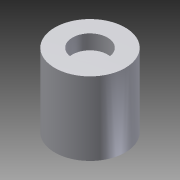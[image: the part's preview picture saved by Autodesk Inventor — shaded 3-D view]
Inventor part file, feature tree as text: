
AUTODESK INVENTOR PART (.ipt)
format: ipt  version: 2014 SP1 (Build 180222100, 222)  size: 105,472 bytes
history: native  units: mm
features: extrude x7, sketch x7
ambient origin geometry x8: Origin, YZ Plane, XZ Plane, XY Plane, X Axis, Y Axis, Z Axis, Center Point
bodies: Solid1 (feature_tree)
feature tree (14):
  extrude  "Extrusion1"  Depth=15.0mm TaperAngle=0.0deg
  extrude  "Extrusion2"  Depth=7.0mm TaperAngle=0.0deg
  extrude  "Extrusion3"  Depth=2.5mm TaperAngle=0.0deg
  extrude  "Extrusion4"  Depth=15.0mm TaperAngle=0.0deg
  extrude  "Extrusion5"  Depth=17.5mm TaperAngle=0.0deg
  extrude  "Extrusion6"  [1 undecoded]
  extrude  "Extrusion7"  [1 undecoded]
  sketch  "Sketch1"  dims[d0=12.0mm d1=15.0mm d2=0.0mm]
  sketch  "Sketch2"  dims[d3=9.398mm d4=7.0mm d5=0.0mm]
  sketch  "Sketch3"  dims[d6=6.0mm d7=2.5mm d8=0.0mm]
  sketch  "Sketch4"  dims[d9=15.0mm d10=0.0mm d11=15.0mm d12=0.0mm]
  sketch  "Sketch5"  dims[d13=17.5mm d14=0.0mm d15=17.5mm d16=0.0mm]
  sketch  "Sketch6"
  sketch  "Sketch7"
note: 2 required parameter values undecoded (feature->parameter linkage not recoverable at this tier; creation-order binding heuristic only, values carry confidence <= 0.55)
